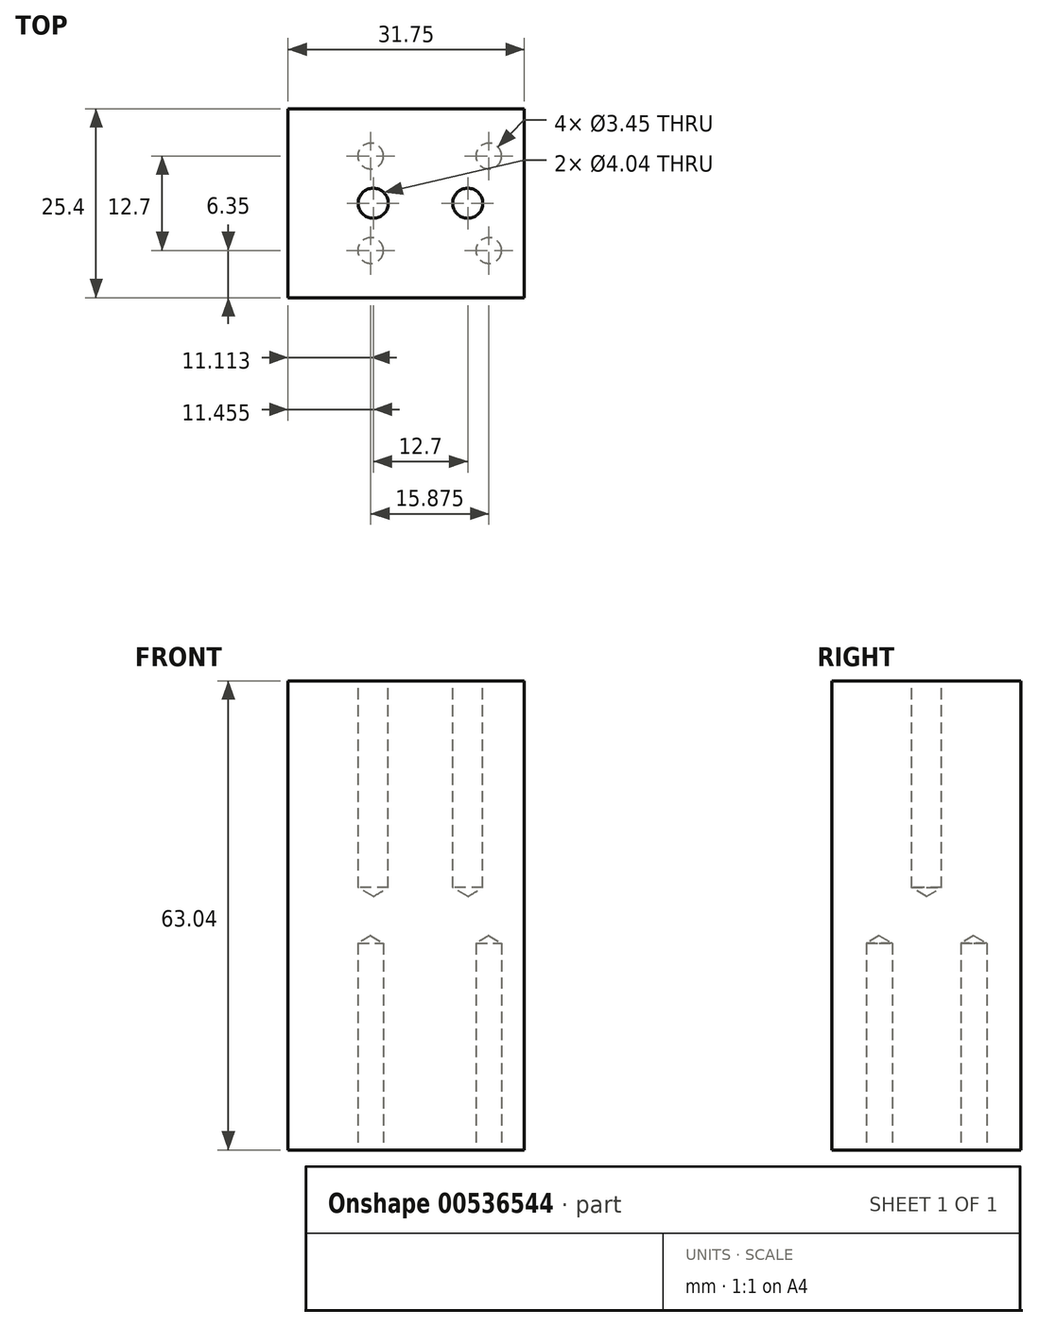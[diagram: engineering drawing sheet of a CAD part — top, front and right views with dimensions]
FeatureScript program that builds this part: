
annotation { "Feature Type Name" : "Feature", "Feature Type Description" : "" }
export const myFeature = defineFeature(function(context is Context, id is Id, definition is map)
    precondition{}
    {
        {
            var Q0;
            Q0=qCreatedBy(makeId("Front.planeOp"),FACE);
            var sketch = newSketch(context, id + "F0", { "sketchPlane" : qUnion([Q0])});
            skLineSegment(sketch, "E0.bottom", {"start": v(0, 0) * mm, "end": v(-31.75, 0) * mm});
            skLineSegment(sketch, "E0.top", {"start": v(0, 63.04) * mm, "end": v(-31.75, 63.04) * mm});
            skLineSegment(sketch, "E0.left", {"start": v(0, 0) * mm, "end": v(0, 63.04) * mm});
            skLineSegment(sketch, "E0.right", {"start": v(-31.75, 0) * mm, "end": v(-31.75, 63.04) * mm});
            skSolve(sketch);
        }
        {
            var Q0;
            Q0 = qSketchRegion(id + "F0", true);
            extrude(context, id + "F1", {"entities" : qUnion([Q0]), "endBound" : BoundingType.SYMMETRIC, "depth" : 25.4 * mm, "offsetDistance" : 25.4 * mm});
        }
        {
            var Q0;
            Q0=makeQuery(id+"F1.opExtrude","SWEPT_FACE",FACE,{"disambiguationData":[OSD([sQuery(id+"F0.wireOp",EDGE,"E0.bottom")])]});
            var sketch = newSketch(context, id + "F2", { "sketchPlane" : qUnion([Q0])});
            skLineSegment(sketch, "E1.bottom", {"start": v(-20.64, 6.35) * mm, "end": v(-4.76, 6.35) * mm, "construction": true});
            skLineSegment(sketch, "E1.top", {"start": v(-20.64, -6.35) * mm, "end": v(-4.76, -6.35) * mm, "construction": true});
            skLineSegment(sketch, "E1.left", {"start": v(-20.64, 6.35) * mm, "end": v(-20.64, -6.35) * mm, "construction": true});
            skLineSegment(sketch, "E1.right", {"start": v(-4.76, 6.35) * mm, "end": v(-4.76, -6.35) * mm, "construction": true});
            skLineSegment(sketch, "E2", {"start": v(-4.76, 0) * mm, "end": v(0, 0) * mm, "construction": true});
            skPoint(sketch, "E3", {"position": v(-12.7, 6.35) * mm});
            skSolve(sketch);
        }
        {
            var Q0;
            Q0=sQuery(id+"F2.wireOp",VERTEX,"E1.bottom.start");
            var Q1;
            Q1=sQuery(id+"F2.wireOp",VERTEX,"E1.right.start");
            var Q2;
            Q2=sQuery(id+"F2.wireOp",VERTEX,"E1.right.end");
            var Q3;
            Q3=sQuery(id+"F2.wireOp",VERTEX,"E1.left.end");
            var Q4;
            Q4=makeQuery(id+"F1.opExtrude","SWEPT_BODY",BODY,{"disambiguationData":[OSD([sQuery(id+"F0.wireOp",EDGE,"E0.bottom"),sQuery(id+"F0.wireOp",EDGE,"E0.top"),sQuery(id+"F0.wireOp",EDGE,"E0.left"),sQuery(id+"F0.wireOp",EDGE,"E0.right")])]});
            hole(context, id + "F3", {"style" : HoleStyle.SIMPLE, "endStyle" : HoleEndStyle.BLIND, "standardTappedOrClearance" : lookupTablePath({ "standard" : "ANSI", "engagement" : "75%", "pitch" : "32 tpi", "size" : "#8", "type" : "Tapped" }), "standardBlindInLast" : lookupTablePath({ "standard" : "ANSI", "engagement" : "75%", "pitch" : "32 tpi", "size" : "#8", "type" : "Tapped" }), "holeDiameter" : 3.45 * mm, "showTappedDepth" : true, "holeDepth" : 27.78 * mm, "tappedDepth" : 25.4 * mm, "tapClearance" : 3, "startFromSketch" : true, "locations" : qUnion([Q0, Q1, Q2, Q3]), "scope" : qUnion([Q4]), "majorDiameter" : 4.17 * mm});
        }
        {
            var Q0;
            Q0=makeQuery(id+"F1.opExtrude","SWEPT_FACE",FACE,{"disambiguationData":[OSD([sQuery(id+"F0.wireOp",EDGE,"E0.top")])]});
            var sketch = newSketch(context, id + "F4", { "sketchPlane" : qUnion([Q0])});
            skLineSegment(sketch, "E4", {"start": v(0, 0) * mm, "end": v(-7.6, 0) * mm, "construction": true});
            skPoint(sketch, "E4.endSnap0", {"position": v(0, 0) * mm});
            skLineSegment(sketch, "E5", {"start": v(-7.6, 0) * mm, "end": v(-20.3, 0) * mm, "construction": true});
            skSolve(sketch);
        }
        {
            var Q0;
            Q0=sQuery(id+"F4.wireOp",VERTEX,"E4.end");
            var Q1;
            Q1=sQuery(id+"F4.wireOp",VERTEX,"E5.end");
            var Q2;
            Q2=makeQuery(id+"F1.opExtrude","SWEPT_BODY",BODY,{"disambiguationData":[OSD([sQuery(id+"F0.wireOp",EDGE,"E0.bottom"),sQuery(id+"F0.wireOp",EDGE,"E0.top"),sQuery(id+"F0.wireOp",EDGE,"E0.left"),sQuery(id+"F0.wireOp",EDGE,"E0.right")])]});
            hole(context, id + "F5", {"style" : HoleStyle.SIMPLE, "endStyle" : HoleEndStyle.BLIND, "standardTappedOrClearance" : lookupTablePath({ "standard" : "ANSI", "engagement" : "75%", "pitch" : "32 tpi", "size" : "#10", "type" : "Tapped" }), "standardBlindInLast" : lookupTablePath({ "standard" : "ANSI", "engagement" : "75%", "pitch" : "32 tpi", "size" : "#10", "type" : "Tapped" }), "holeDiameter" : 4.04 * mm, "showTappedDepth" : true, "holeDepth" : 27.78 * mm, "tappedDepth" : 25.4 * mm, "tapClearance" : 3, "startFromSketch" : true, "locations" : qUnion([Q0, Q1]), "scope" : qUnion([Q2]), "majorDiameter" : 4.83 * mm});
        }
    });
